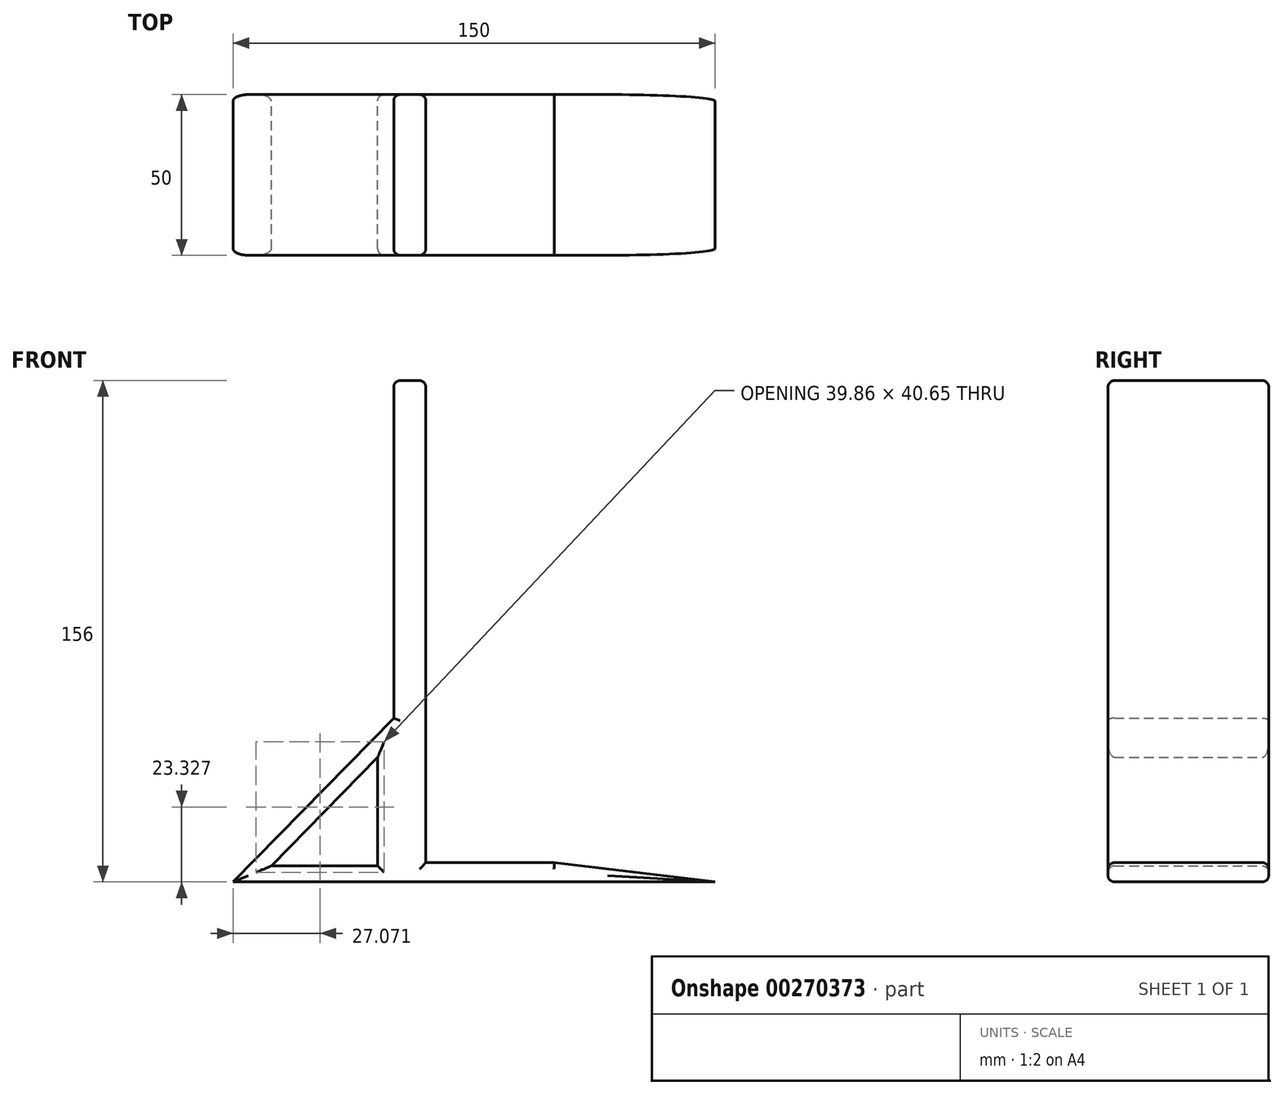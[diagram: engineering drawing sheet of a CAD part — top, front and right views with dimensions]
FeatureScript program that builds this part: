
annotation { "Feature Type Name" : "Feature", "Feature Type Description" : "" }
export const myFeature = defineFeature(function(context is Context, id is Id, definition is map)
    precondition{}
    {
        {
            var Q0;
            Q0=qCreatedBy(makeId("Front.planeOp"),FACE);
            var sketch = newSketch(context, id + "F0", { "sketchPlane" : qUnion([Q0])});
            skLineSegment(sketch, "E0.bottom", {"start": v(0, 0) * mm, "end": v(10, 0) * mm});
            skLineSegment(sketch, "E0.top", {"start": v(0, 150) * mm, "end": v(10, 150) * mm});
            skLineSegment(sketch, "E0.left", {"start": v(0, 0) * mm, "end": v(0, 150) * mm});
            skLineSegment(sketch, "E0.right", {"start": v(10, 0) * mm, "end": v(10, 150) * mm});
            skLineSegment(sketch, "E1.bottom", {"start": v(10, 0) * mm, "end": v(50, 0) * mm});
            skLineSegment(sketch, "E1.top", {"start": v(0, -6) * mm, "end": v(100, -6) * mm});
            skLineSegment(sketch, "E1.left", {"start": v(0, 0) * mm, "end": v(0, -6) * mm});
            skLineSegment(sketch, "E2", {"start": v(0, -6) * mm, "end": v(-50, -6) * mm});
            skLineSegment(sketch, "E3", {"start": v(-50, -6) * mm, "end": v(0, 45) * mm});
            skLineSegment(sketch, "E4", {"start": v(50, 0) * mm, "end": v(100, -6) * mm});
            skLineSegment(sketch, "E5", {"start": v(0, -6) * mm, "end": v(0, 45) * mm});
            skLineSegment(sketch, "E6.0", {"start": v(-5, -1) * mm, "end": v(-5, 32.76) * mm});
            skLineSegment(sketch, "E6.1", {"start": v(-5, -1) * mm, "end": v(-38.1, -1) * mm});
            skLineSegment(sketch, "E6.2", {"start": v(-38.1, -1) * mm, "end": v(-5, 32.76) * mm});
            skSolve(sketch);
        }
        {
            var Q0;
            {var subQ1=sQuery(id+"F0.wireOp",EDGE,"E0.bottom");Q0=makeQuery(id+"F0.imprint","IMPRINT",FACE,{"disambiguationData":[TD([[makeQuery(id+"F0.imprint","IMPRINT",EDGE,{"derivedFrom":subQ1}),1.0]])]});}
            var Q1;
            {var subQ3=sQuery(id+"F0.wireOp",EDGE,"E2");Q1=makeQuery(id+"F0.imprint","IMPRINT",FACE,{"disambiguationData":[TD([[makeQuery(id+"F0.imprint","IMPRINT",EDGE,{"derivedFrom":subQ3}),-1.0]])]});}
            var Q2;
            {var subQ1=sQuery(id+"F0.wireOp",EDGE,"E0.bottom");Q2=makeQuery(id+"F0.imprint","IMPRINT",FACE,{"disambiguationData":[TD([[makeQuery(id+"F0.imprint","IMPRINT",EDGE,{"derivedFrom":subQ1}),-1.0]])]});}
            extrude(context, id + "F1", {"entities" : qUnion([Q0, Q1, Q2]), "depth" : 50 * mm});
        }
        {
            var Q0;
            Q0=makeQuery(id+"F1.opExtrude","CAP_FACE",FACE,{"disambiguationData":[OSD([sQuery(id+"F0.wireOp",EDGE,"E0.top"),sQuery(id+"F0.wireOp",EDGE,"E0.left"),sQuery(id+"F0.wireOp",EDGE,"E0.right"),sQuery(id+"F0.wireOp",EDGE,"E1.bottom"),sQuery(id+"F0.wireOp",EDGE,"E1.top"),sQuery(id+"F0.wireOp",EDGE,"E2"),sQuery(id+"F0.wireOp",EDGE,"E3"),sQuery(id+"F0.wireOp",EDGE,"E4")])],"isStart":false});
            var Q1;
            Q1=makeQuery(id+"F1.opExtrude","CAP_FACE",FACE,{"disambiguationData":[OSD([sQuery(id+"F0.wireOp",EDGE,"E0.top"),sQuery(id+"F0.wireOp",EDGE,"E0.left"),sQuery(id+"F0.wireOp",EDGE,"E0.right"),sQuery(id+"F0.wireOp",EDGE,"E1.bottom"),sQuery(id+"F0.wireOp",EDGE,"E1.top"),sQuery(id+"F0.wireOp",EDGE,"E2"),sQuery(id+"F0.wireOp",EDGE,"E3"),sQuery(id+"F0.wireOp",EDGE,"E4")])],"isStart":true});
            var Q2;
            Q2=makeQuery(id+"F1.opExtrude","SWEPT_FACE",FACE,{"disambiguationData":[OSD([sQuery(id+"F0.wireOp",EDGE,"E0.top")])]});
            fillet(context, id + "F2", {"entities" : qUnion([Q0, Q1, Q2]), "radius" : 2 * mm, "tangentPropagation" : true, "allowEdgeOverflow" : false});
        }
    });
